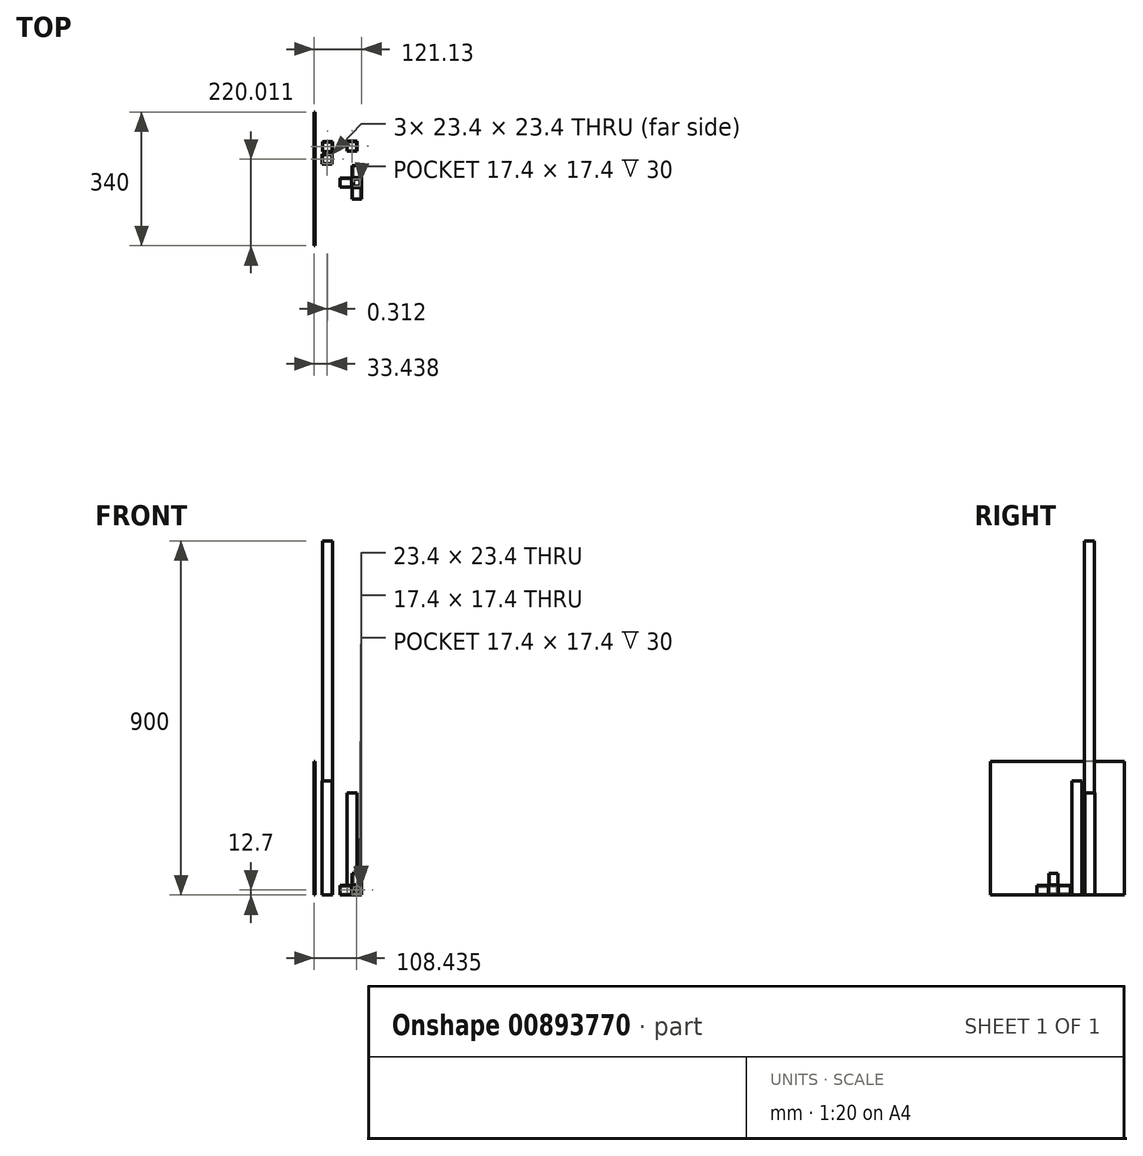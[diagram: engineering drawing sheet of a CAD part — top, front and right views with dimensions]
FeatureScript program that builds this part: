
annotation { "Feature Type Name" : "Feature", "Feature Type Description" : "" }
export const myFeature = defineFeature(function(context is Context, id is Id, definition is map)
    precondition{}
    {
        {
            var Q0;
            Q0=qCreatedBy(makeId("Top.planeOp"),FACE);
            var sketch = newSketch(context, id + "F0", { "sketchPlane" : qUnion([Q0])});
            skLineSegment(sketch, "E0.bottom", {"start": v(-46.92, 33.18) * mm, "end": v(-21.52, 33.18) * mm});
            skLineSegment(sketch, "E0.top", {"start": v(-46.92, 7.78) * mm, "end": v(-21.52, 7.78) * mm});
            skLineSegment(sketch, "E0.left", {"start": v(-46.92, 33.18) * mm, "end": v(-46.92, 7.78) * mm});
            skLineSegment(sketch, "E0.right", {"start": v(-21.52, 33.18) * mm, "end": v(-21.52, 7.78) * mm});
            skLineSegment(sketch, "E1.bottom", {"start": v(-45.92, 32.18) * mm, "end": v(-22.52, 32.18) * mm});
            skLineSegment(sketch, "E1.top", {"start": v(-45.92, 8.78) * mm, "end": v(-22.52, 8.78) * mm});
            skLineSegment(sketch, "E1.left", {"start": v(-45.92, 32.18) * mm, "end": v(-45.92, 8.78) * mm});
            skLineSegment(sketch, "E1.right", {"start": v(-22.52, 32.18) * mm, "end": v(-22.52, 8.78) * mm});
            skSolve(sketch);
        }
        {
            var Q0;
            Q0 = qSketchRegion(id + "F0", true);
            extrude(context, id + "F1", {"entities" : qUnion([Q0]), "depth" : 290 * mm, "offsetDistance" : 25 * mm});
        }
        {
            var Q0;
            Q0=qCreatedBy(makeId("Top.planeOp"),FACE);
            var sketch = newSketch(context, id + "F2", { "sketchPlane" : qUnion([Q0])});
            skLineSegment(sketch, "E2.bottom", {"start": v(-46.61, 64.42) * mm, "end": v(-21.21, 64.42) * mm});
            skLineSegment(sketch, "E2.top", {"start": v(-46.61, 39.02) * mm, "end": v(-21.21, 39.02) * mm});
            skLineSegment(sketch, "E2.left", {"start": v(-46.61, 64.42) * mm, "end": v(-46.61, 39.02) * mm});
            skLineSegment(sketch, "E2.right", {"start": v(-21.21, 64.42) * mm, "end": v(-21.21, 39.02) * mm});
            skLineSegment(sketch, "E3.bottom", {"start": v(-45.61, 63.42) * mm, "end": v(-22.21, 63.42) * mm});
            skLineSegment(sketch, "E3.top", {"start": v(-45.61, 40.02) * mm, "end": v(-22.21, 40.02) * mm});
            skLineSegment(sketch, "E3.left", {"start": v(-45.61, 63.42) * mm, "end": v(-45.61, 40.02) * mm});
            skLineSegment(sketch, "E3.right", {"start": v(-22.21, 63.42) * mm, "end": v(-22.21, 40.02) * mm});
            skSolve(sketch);
        }
        {
            var Q0;
            Q0 = qSketchRegion(id + "F2", true);
            extrude(context, id + "F3", {"entities" : qUnion([Q0]), "depth" : 900 * mm, "offsetDistance" : 25 * mm});
        }
        {
            var Q0;
            Q0=qCreatedBy(makeId("Top.planeOp"),FACE);
            var sketch = newSketch(context, id + "F4", { "sketchPlane" : qUnion([Q0])});
            skLineSegment(sketch, "E4.bottom", {"start": v(28.07, -26.23) * mm, "end": v(53.47, -26.23) * mm});
            skLineSegment(sketch, "E4.top", {"start": v(28.07, -51.63) * mm, "end": v(53.47, -51.63) * mm});
            skLineSegment(sketch, "E4.left", {"start": v(28.07, -26.23) * mm, "end": v(28.07, -51.63) * mm});
            skLineSegment(sketch, "E4.right", {"start": v(53.47, -26.23) * mm, "end": v(53.47, -51.63) * mm});
            skSolve(sketch);
        }
        {
            var Q0;
            Q0=makeQuery(id+"F4.imprint","IMPRINT",FACE,{"disambiguationData":[TD([[makeQuery(id+"F4.imprint","IMPRINT",EDGE,{"derivedFrom":sQuery(id+"F4.wireOp",EDGE,"E4.bottom")}),-1.0]])]});
            extrude(context, id + "F5", {"entities" : qUnion([Q0]), "depth" : 25.4 * mm, "offsetDistance" : 25 * mm});
        }
        {
            var Q0;
            Q0=makeQuery(id+"F5.opExtrude","CAP_FACE",FACE,{"disambiguationData":[OSD([sQuery(id+"F4.wireOp",EDGE,"E4.bottom"),sQuery(id+"F4.wireOp",EDGE,"E4.top"),sQuery(id+"F4.wireOp",EDGE,"E4.left"),sQuery(id+"F4.wireOp",EDGE,"E4.right")])],"isStart":false});
            var sketch = newSketch(context, id + "F6", { "sketchPlane" : qUnion([Q0])});
            skLineSegment(sketch, "E5.bottom", {"start": v(29.07, -27.23) * mm, "end": v(52.47, -27.23) * mm});
            skLineSegment(sketch, "E5.top", {"start": v(29.07, -50.63) * mm, "end": v(52.47, -50.63) * mm});
            skLineSegment(sketch, "E5.left", {"start": v(29.07, -27.23) * mm, "end": v(29.07, -50.63) * mm});
            skLineSegment(sketch, "E5.right", {"start": v(52.47, -27.23) * mm, "end": v(52.47, -50.63) * mm});
            skLineSegment(sketch, "E6.bottom", {"start": v(32.07, -30.23) * mm, "end": v(49.47, -30.23) * mm});
            skLineSegment(sketch, "E6.top", {"start": v(32.07, -47.63) * mm, "end": v(49.47, -47.63) * mm});
            skLineSegment(sketch, "E6.left", {"start": v(32.07, -30.23) * mm, "end": v(32.07, -47.63) * mm});
            skLineSegment(sketch, "E6.right", {"start": v(49.47, -30.23) * mm, "end": v(49.47, -47.63) * mm});
            skSolve(sketch);
        }
        {
            var Q0;
            Q0 = qSketchRegion(id + "F6", true);
            extrude(context, id + "F7", {"entities" : qUnion([Q0]), "operationType" : NewBodyOperationType.ADD, "depth" : 30 * mm, "offsetDistance" : 25 * mm});
        }
        {
            var Q0;
            Q0=makeQuery(id+"F5.opExtrude","SWEPT_FACE",FACE,{"disambiguationData":[OSD([sQuery(id+"F4.wireOp",EDGE,"E4.left")])]});
            var sketch = newSketch(context, id + "F8", { "sketchPlane" : qUnion([Q0])});
            skLineSegment(sketch, "E7.bottom", {"start": v(27.23, 1) * mm, "end": v(50.63, 1) * mm});
            skLineSegment(sketch, "E7.top", {"start": v(27.23, 24.4) * mm, "end": v(50.63, 24.4) * mm});
            skLineSegment(sketch, "E7.left", {"start": v(27.23, 1) * mm, "end": v(27.23, 24.4) * mm});
            skLineSegment(sketch, "E7.right", {"start": v(50.63, 1) * mm, "end": v(50.63, 24.4) * mm});
            skLineSegment(sketch, "E8.bottom", {"start": v(30.23, 4) * mm, "end": v(47.63, 4) * mm});
            skLineSegment(sketch, "E8.top", {"start": v(30.23, 21.4) * mm, "end": v(47.63, 21.4) * mm});
            skLineSegment(sketch, "E8.left", {"start": v(30.23, 4) * mm, "end": v(30.23, 21.4) * mm});
            skLineSegment(sketch, "E8.right", {"start": v(47.63, 4) * mm, "end": v(47.63, 21.4) * mm});
            skSolve(sketch);
        }
        {
            var Q0;
            Q0 = qSketchRegion(id + "F8", true);
            extrude(context, id + "F9", {"entities" : qUnion([Q0]), "operationType" : NewBodyOperationType.ADD, "depth" : 30 * mm, "offsetDistance" : 25 * mm});
        }
        {
            var Q0;
            Q0=makeQuery(id+"F5.opExtrude","SWEPT_FACE",FACE,{"disambiguationData":[OSD([sQuery(id+"F4.wireOp",EDGE,"E4.top")])]});
            var sketch = newSketch(context, id + "F10", { "sketchPlane" : qUnion([Q0])});
            skLineSegment(sketch, "E9.bottom", {"start": v(29.07, 24.4) * mm, "end": v(52.47, 24.4) * mm});
            skLineSegment(sketch, "E9.top", {"start": v(29.07, 1) * mm, "end": v(52.47, 1) * mm});
            skLineSegment(sketch, "E9.left", {"start": v(29.07, 24.4) * mm, "end": v(29.07, 1) * mm});
            skLineSegment(sketch, "E9.right", {"start": v(52.47, 24.4) * mm, "end": v(52.47, 1) * mm});
            skLineSegment(sketch, "E10.bottom", {"start": v(32.07, 21.4) * mm, "end": v(49.47, 21.4) * mm});
            skLineSegment(sketch, "E10.top", {"start": v(32.07, 4) * mm, "end": v(49.47, 4) * mm});
            skLineSegment(sketch, "E10.left", {"start": v(32.07, 21.4) * mm, "end": v(32.07, 4) * mm});
            skLineSegment(sketch, "E10.right", {"start": v(49.47, 21.4) * mm, "end": v(49.47, 4) * mm});
            skSolve(sketch);
        }
        {
            var Q0;
            Q0 = qSketchRegion(id + "F10", true);
            extrude(context, id + "F11", {"entities" : qUnion([Q0]), "operationType" : NewBodyOperationType.ADD, "depth" : 30 * mm, "offsetDistance" : 25 * mm});
        }
        {
            var Q0;
            Q0=makeQuery(id+"F5.opExtrude","SWEPT_FACE",FACE,{"disambiguationData":[OSD([sQuery(id+"F4.wireOp",EDGE,"E4.bottom")])]});
            var sketch = newSketch(context, id + "F12", { "sketchPlane" : qUnion([Q0])});
            skLineSegment(sketch, "E11.bottom", {"start": v(-52.47, 24.4) * mm, "end": v(-29.07, 24.4) * mm});
            skLineSegment(sketch, "E11.top", {"start": v(-52.47, 1) * mm, "end": v(-29.07, 1) * mm});
            skLineSegment(sketch, "E11.left", {"start": v(-52.47, 24.4) * mm, "end": v(-52.47, 1) * mm});
            skLineSegment(sketch, "E11.right", {"start": v(-29.07, 24.4) * mm, "end": v(-29.07, 1) * mm});
            skLineSegment(sketch, "E12.bottom", {"start": v(-49.47, 21.4) * mm, "end": v(-32.07, 21.4) * mm});
            skLineSegment(sketch, "E12.top", {"start": v(-49.47, 4) * mm, "end": v(-32.07, 4) * mm});
            skLineSegment(sketch, "E12.left", {"start": v(-49.47, 21.4) * mm, "end": v(-49.47, 4) * mm});
            skLineSegment(sketch, "E12.right", {"start": v(-32.07, 21.4) * mm, "end": v(-32.07, 4) * mm});
            skSolve(sketch);
        }
        {
            var Q0;
            Q0 = qSketchRegion(id + "F12", true);
            extrude(context, id + "F13", {"entities" : qUnion([Q0]), "operationType" : NewBodyOperationType.ADD, "depth" : 30 * mm, "offsetDistance" : 25 * mm});
        }
        {
            var Q0;
            Q0=qCreatedBy(makeId("Top.planeOp"),FACE);
            var sketch = newSketch(context, id + "F14", { "sketchPlane" : qUnion([Q0])});
            skLineSegment(sketch, "E13.bottom", {"start": v(15.65, 65.6) * mm, "end": v(41.05, 65.6) * mm});
            skLineSegment(sketch, "E13.top", {"start": v(15.65, 40.2) * mm, "end": v(41.05, 40.2) * mm});
            skLineSegment(sketch, "E13.left", {"start": v(15.65, 65.6) * mm, "end": v(15.65, 40.2) * mm});
            skLineSegment(sketch, "E13.right", {"start": v(41.05, 65.6) * mm, "end": v(41.05, 40.2) * mm});
            skLineSegment(sketch, "E14.bottom", {"start": v(16.65, 64.6) * mm, "end": v(40.05, 64.6) * mm});
            skLineSegment(sketch, "E14.top", {"start": v(16.65, 41.2) * mm, "end": v(40.05, 41.2) * mm});
            skLineSegment(sketch, "E14.left", {"start": v(16.65, 64.6) * mm, "end": v(16.65, 41.2) * mm});
            skLineSegment(sketch, "E14.right", {"start": v(40.05, 64.6) * mm, "end": v(40.05, 41.2) * mm});
            skSolve(sketch);
        }
        {
            var Q0;
            Q0 = qSketchRegion(id + "F14", true);
            extrude(context, id + "F15", {"entities" : qUnion([Q0]), "depth" : 260 * mm, "offsetDistance" : 25 * mm});
        }
        {
            var Q0;
            Q0=qCreatedBy(makeId("Top.planeOp"),FACE);
            var sketch = newSketch(context, id + "F16", { "sketchPlane" : qUnion([Q0])});
            skLineSegment(sketch, "E15.bottom", {"start": v(-67.66, 140.47) * mm, "end": v(-64.66, 140.47) * mm});
            skLineSegment(sketch, "E15.top", {"start": v(-67.66, -199.53) * mm, "end": v(-64.66, -199.53) * mm});
            skLineSegment(sketch, "E15.left", {"start": v(-67.66, 140.47) * mm, "end": v(-67.66, -199.53) * mm});
            skLineSegment(sketch, "E15.right", {"start": v(-64.66, 140.47) * mm, "end": v(-64.66, -199.53) * mm});
            skSolve(sketch);
        }
        {
            var Q0;
            Q0 = qSketchRegion(id + "F16", true);
            extrude(context, id + "F17", {"entities" : qUnion([Q0]), "depth" : 340 * mm, "offsetDistance" : 25 * mm});
        }
    });
